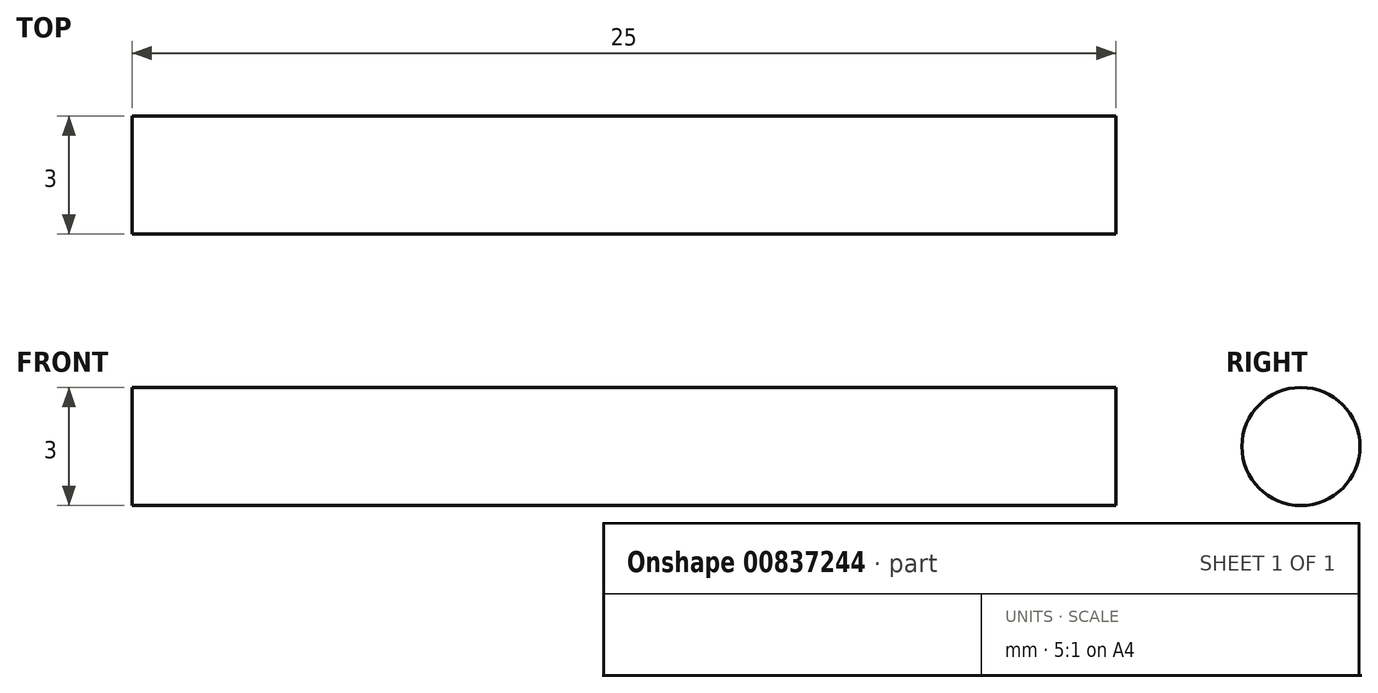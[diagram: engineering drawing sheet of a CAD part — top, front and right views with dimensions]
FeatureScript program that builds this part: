
annotation { "Feature Type Name" : "Feature", "Feature Type Description" : "" }
export const myFeature = defineFeature(function(context is Context, id is Id, definition is map)
    precondition{}
    {
        {
            var Q0;
            Q0=qCreatedBy(makeId("Right.planeOp"),FACE);
            var sketch = newSketch(context, id + "F0", { "sketchPlane" : qUnion([Q0])});
            skCircle(sketch, "E0", {"center": v(0, 0) * mm, "radius": 1.5 * mm});
            skSolve(sketch);
        }
        {
            var Q0;
            Q0 = qSketchRegion(id + "F0", true);
            extrude(context, id + "F1", {"entities" : qUnion([Q0]), "depth" : 25 * mm, "offsetDistance" : 25.4 * mm});
        }
    });
